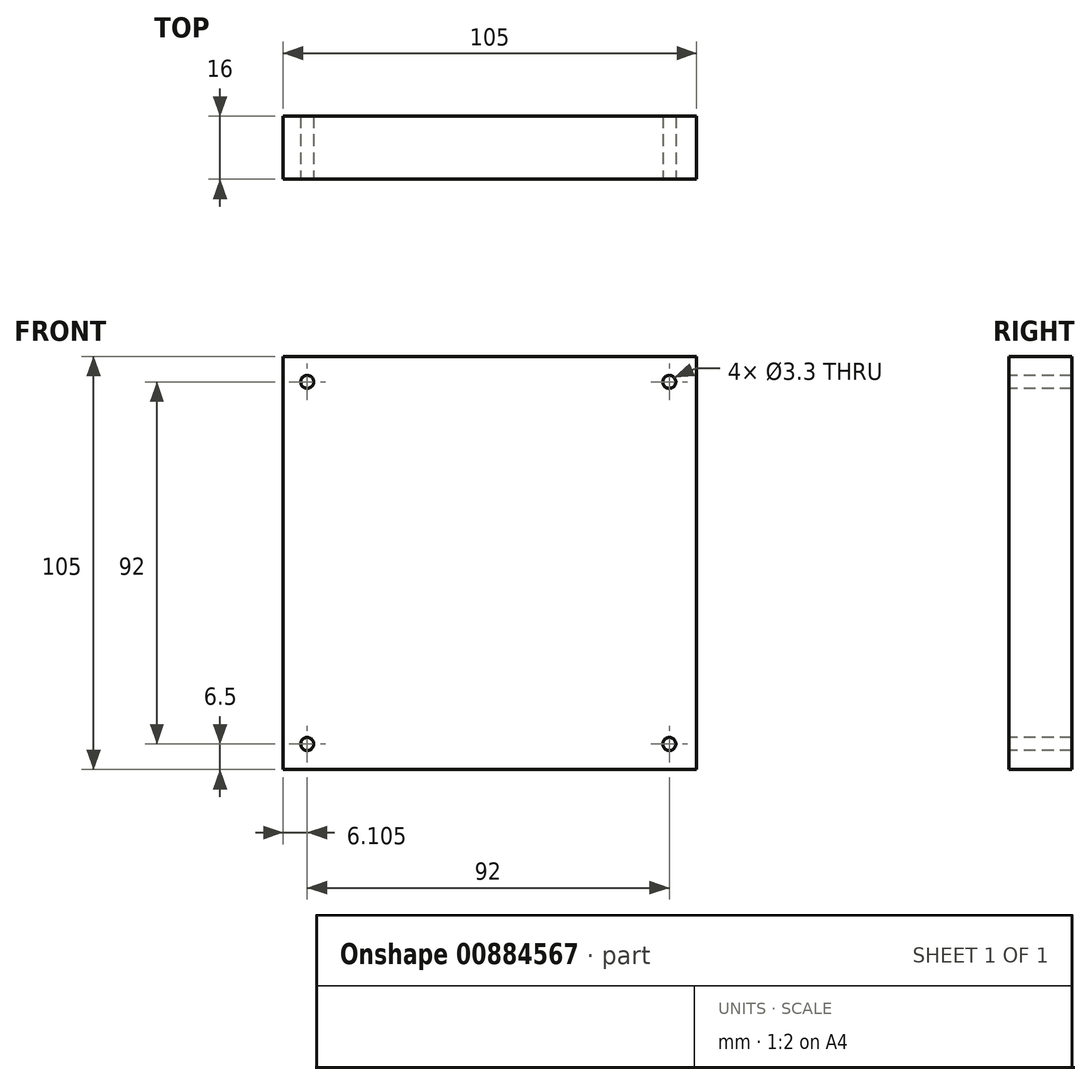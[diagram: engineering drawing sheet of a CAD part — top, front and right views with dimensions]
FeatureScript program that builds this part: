
annotation { "Feature Type Name" : "Feature", "Feature Type Description" : "" }
export const myFeature = defineFeature(function(context is Context, id is Id, definition is map)
    precondition{}
    {
        {
            var Q0;
            Q0=qCreatedBy(makeId("Front.planeOp"),FACE);
            var sketch = newSketch(context, id + "F0", { "sketchPlane" : qUnion([Q0])});
            skLineSegment(sketch, "E0.bottom", {"start": v(52.5, -52.5) * mm, "end": v(-52.5, -52.5) * mm});
            skLineSegment(sketch, "E0.top", {"start": v(52.5, 52.5) * mm, "end": v(-52.5, 52.5) * mm});
            skLineSegment(sketch, "E0.left", {"start": v(52.5, -52.5) * mm, "end": v(52.5, 52.5) * mm});
            skLineSegment(sketch, "E0.right", {"start": v(-52.5, -52.5) * mm, "end": v(-52.5, 52.5) * mm});
            skPoint(sketch, "E0.middle", {"position": v(0, 0) * mm});
            skSolve(sketch);
        }
        {
            var Q0;
            Q0=makeQuery(id+"F0.imprint","IMPRINT",FACE,{"disambiguationData":[TD([[makeQuery(id+"F0.imprint","IMPRINT",EDGE,{"derivedFrom":sQuery(id+"F0.wireOp",EDGE,"E0.bottom")}),-1.0]])]});
            extrude(context, id + "F1", {"entities" : qUnion([Q0]), "depth" : 16 * mm, "offsetDistance" : 25 * mm});
        }
        {
            var Q0;
            Q0=makeQuery(id+"F1.opExtrude","CAP_FACE",FACE,{"disambiguationData":[OSD([sQuery(id+"F0.wireOp",EDGE,"E0.bottom"),sQuery(id+"F0.wireOp",EDGE,"E0.top"),sQuery(id+"F0.wireOp",EDGE,"E0.left"),sQuery(id+"F0.wireOp",EDGE,"E0.right")])],"isStart":false});
            var sketch = newSketch(context, id + "F2", { "sketchPlane" : qUnion([Q0])});
            skPoint(sketch, "E1", {"position": v(-46.4, 46) * mm});
            skPoint(sketch, "E2", {"position": v(45.6, 46) * mm});
            skPoint(sketch, "E3", {"position": v(-46.4, -46) * mm});
            skPoint(sketch, "E4", {"position": v(45.6, -46) * mm});
            skSolve(sketch);
        }
        {
            var Q0;
            Q0=sQuery(id+"F2.wireOp",VERTEX,"E1");
            var Q1;
            Q1=sQuery(id+"F2.wireOp",VERTEX,"E2");
            var Q2;
            Q2=sQuery(id+"F2.wireOp",VERTEX,"E3");
            var Q3;
            Q3=sQuery(id+"F2.wireOp",VERTEX,"E4");
            var Q4;
            Q4=makeQuery(id+"F1.opExtrude","SWEPT_BODY",BODY,{"disambiguationData":[OSD([sQuery(id+"F0.wireOp",EDGE,"E0.bottom"),sQuery(id+"F0.wireOp",EDGE,"E0.top"),sQuery(id+"F0.wireOp",EDGE,"E0.left"),sQuery(id+"F0.wireOp",EDGE,"E0.right")])]});
            hole(context, id + "F3", {"style" : HoleStyle.SIMPLE, "endStyle" : HoleEndStyle.THROUGH, "standardTappedOrClearance" : lookupTablePath({ "standard" : "ISO", "engagement" : "75%", "pitch" : "0.7 mm", "size" : "M4", "type" : "Tapped" }), "standardBlindInLast" : lookupTablePath({ "standard" : "ISO", "engagement" : "75%", "pitch" : "0.7 mm", "size" : "M4", "type" : "Tapped" }), "holeDiameter" : 3.3 * mm, "majorDiameter" : 4 * mm, "showTappedDepth" : true, "isTappedThrough" : true, "tappedDepth" : 5.5 * mm, "tapClearance" : 3, "locations" : qUnion([Q0, Q1, Q2, Q3]), "scope" : qUnion([Q4])});
        }
    });
